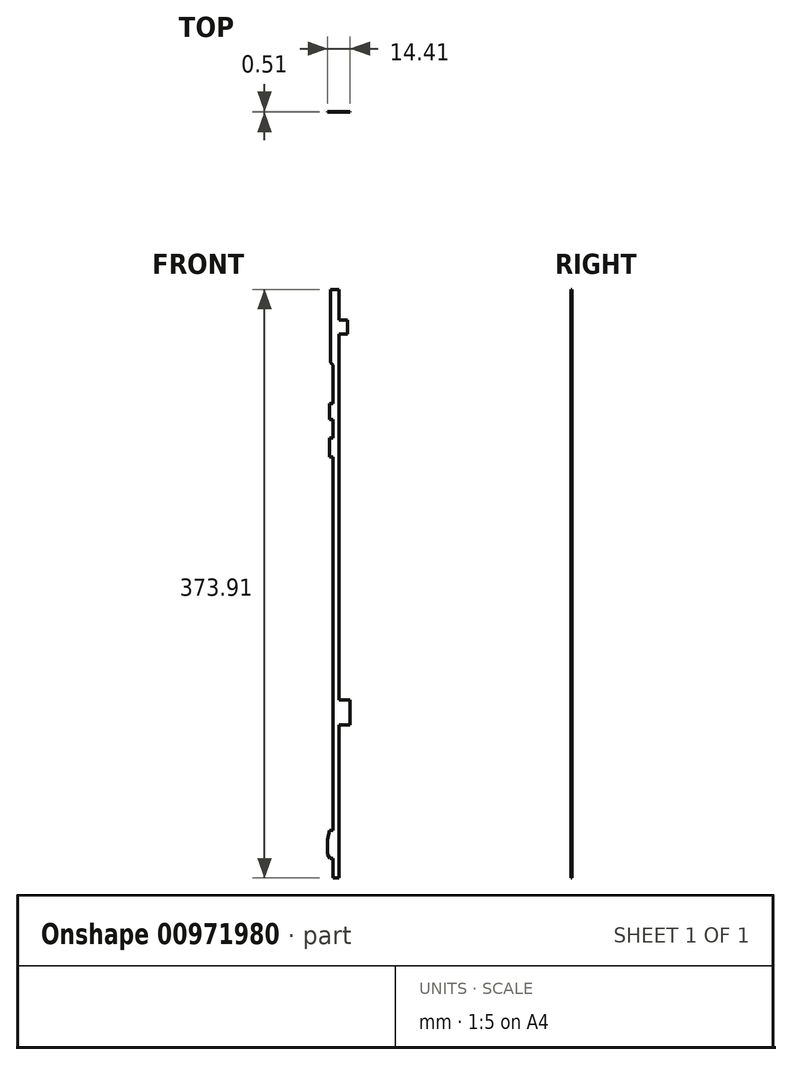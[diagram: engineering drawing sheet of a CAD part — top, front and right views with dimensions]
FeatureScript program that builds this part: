
annotation { "Feature Type Name" : "Feature", "Feature Type Description" : "" }
export const myFeature = defineFeature(function(context is Context, id is Id, definition is map)
    precondition{}
    {
        {
            var Q0;
            Q0=qCreatedBy(makeId("Front.planeOp"),FACE);
            var sketch = newSketch(context, id + "F0", { "sketchPlane" : qUnion([Q0])});
            skLineSegment(sketch, "E0.bottom", {"start": v(2.02, -162.96) * mm, "end": v(-2.02, -162.96) * mm});
            skLineSegment(sketch, "E0.top", {"start": v(2.02, 162.96) * mm, "end": v(-2.02, 162.96) * mm});
            skLineSegment(sketch, "E0.left", {"start": v(2.02, -162.96) * mm, "end": v(2.02, 162.96) * mm});
            skLineSegment(sketch, "E0.right", {"start": v(-2.02, -162.96) * mm, "end": v(-2.02, 162.96) * mm});
            skPoint(sketch, "E0.middle", {"position": v(0, 0) * mm});
            skLineSegment(sketch, "E1", {"start": v(-2.02, 162.96) * mm, "end": v(-3.57, 164.64) * mm});
            skLineSegment(sketch, "E2", {"start": v(-3.57, 164.64) * mm, "end": v(-3.57, 210.95) * mm});
            skLineSegment(sketch, "E3", {"start": v(2.02, 162.96) * mm, "end": v(2.02, 210.95) * mm});
            skLineSegment(sketch, "E4", {"start": v(2.02, 210.95) * mm, "end": v(-3.57, 210.95) * mm});
            skLineSegment(sketch, "E5.bottom", {"start": v(7.35, 191.36) * mm, "end": v(-3.3, 191.36) * mm});
            skLineSegment(sketch, "E5.top", {"start": v(7.35, 182.55) * mm, "end": v(-3.3, 182.55) * mm});
            skLineSegment(sketch, "E5.left", {"start": v(7.35, 191.36) * mm, "end": v(7.35, 182.55) * mm});
            skLineSegment(sketch, "E5.right", {"start": v(-3.3, 191.36) * mm, "end": v(-3.3, 182.55) * mm});
            skPoint(sketch, "E5.middle", {"position": v(2.02, 186.95) * mm});
            skLineSegment(sketch, "E6", {"start": v(-3.57, 138.46) * mm, "end": v(-2.02, 138.46) * mm});
            skLineSegment(sketch, "E7.bottom", {"start": v(-2.02, 138.46) * mm, "end": v(-4.03, 138.46) * mm});
            skLineSegment(sketch, "E7.top", {"start": v(-2.02, 128.28) * mm, "end": v(-4.03, 128.28) * mm});
            skLineSegment(sketch, "E7.left", {"start": v(-2.02, 138.46) * mm, "end": v(-2.02, 128.28) * mm});
            skLineSegment(sketch, "E7.right", {"start": v(-4.03, 138.46) * mm, "end": v(-4.03, 128.28) * mm});
            skLineSegment(sketch, "E8", {"start": v(-2.02, 128.28) * mm, "end": v(-2.02, 116.47) * mm});
            skLineSegment(sketch, "E9.bottom", {"start": v(-2.02, 116.47) * mm, "end": v(-4.03, 116.47) * mm});
            skLineSegment(sketch, "E9.top", {"start": v(-2.02, 104.66) * mm, "end": v(-4.03, 104.66) * mm});
            skLineSegment(sketch, "E9.left", {"start": v(-2.02, 116.47) * mm, "end": v(-2.02, 104.66) * mm});
            skLineSegment(sketch, "E9.right", {"start": v(-4.03, 116.47) * mm, "end": v(-4.03, 104.66) * mm});
            skLineSegment(sketch, "E10.bottom", {"start": v(2.02, -49.96) * mm, "end": v(9.03, -49.96) * mm});
            skLineSegment(sketch, "E10.top", {"start": v(2.02, -65.65) * mm, "end": v(9.03, -65.65) * mm});
            skLineSegment(sketch, "E10.left", {"start": v(2.02, -49.96) * mm, "end": v(2.02, -65.65) * mm});
            skLineSegment(sketch, "E10.right", {"start": v(9.03, -49.96) * mm, "end": v(9.03, -65.65) * mm});
            skLineSegment(sketch, "E11", {"start": v(2.02, -65.65) * mm, "end": v(-2.02, -65.65) * mm});
            skLineSegment(sketch, "E12", {"start": v(-2.02, -65.65) * mm, "end": v(-2.02, -132.81) * mm});
            skLineSegment(sketch, "E13", {"start": v(-2.02, -132.81) * mm, "end": v(-4.03, -132.81) * mm});
            skLineSegment(sketch, "E14", {"start": v(-4.03, -132.81) * mm, "end": v(-5.38, -138.76) * mm});
            skLineSegment(sketch, "E15", {"start": v(-5.38, -138.76) * mm, "end": v(-5.38, -147.79) * mm});
            skLineSegment(sketch, "E16", {"start": v(-5.38, -147.79) * mm, "end": v(-3.72, -150.6) * mm});
            skLineSegment(sketch, "E17", {"start": v(-3.72, -150.6) * mm, "end": v(-2.02, -150.6) * mm});
            skSolve(sketch);
        }
        {
            var Q0;
            Q0=makeQuery(id+"F0.imprint","IMPRINT",FACE,{"disambiguationData":[TD([[makeQuery(id+"F0.imprint","IMPRINT",EDGE,{"derivedFrom":sQuery(id+"F0.wireOp",EDGE,"E10.bottom")}),-1.0]])]});
            var Q1;
            {var subQ0=sQuery(id+"F0.wireOp",EDGE,"E13");Q1=makeQuery(id+"F0.imprint","IMPRINT",FACE,{"disambiguationData":[TD([[makeQuery(id+"F0.imprint","IMPRINT",EDGE,{"derivedFrom":subQ0}),1.0]])]});}
            var Q2;
            {var subQ5=sQuery(id+"F0.wireOp",EDGE,"E5.left");Q2=makeQuery(id+"F0.imprint","IMPRINT",FACE,{"disambiguationData":[TD([[makeQuery(id+"F0.imprint","IMPRINT",EDGE,{"derivedFrom":subQ5}),-1.0]])]});}
            var Q3;
            {var subQ5=sQuery(id+"F0.wireOp",EDGE,"E5.right");Q3=makeQuery(id+"F0.imprint","IMPRINT",FACE,{"disambiguationData":[TD([[makeQuery(id+"F0.imprint","IMPRINT",EDGE,{"derivedFrom":subQ5}),1.0]])]});}
            var Q4;
            {var subQ1=sQuery(id+"F0.wireOp",EDGE,"E0.top");Q4=makeQuery(id+"F0.imprint","IMPRINT",FACE,{"disambiguationData":[TD([[makeQuery(id+"F0.imprint","IMPRINT",EDGE,{"derivedFrom":subQ1}),-1.0]])]});}
            var Q5;
            {var subQ1=sQuery(id+"F0.wireOp",EDGE,"E0.top");Q5=makeQuery(id+"F0.imprint","IMPRINT",FACE,{"disambiguationData":[TD([[makeQuery(id+"F0.imprint","IMPRINT",EDGE,{"derivedFrom":subQ1}),1.0]])]});}
            var Q6;
            Q6=makeQuery(id+"F0.imprint","IMPRINT",FACE,{"disambiguationData":[TD([[makeQuery(id+"F0.imprint","IMPRINT",EDGE,{"derivedFrom":sQuery(id+"F0.wireOp",EDGE,"E9.bottom")}),1.0]])]});
            var Q7;
            {var subQ1=sQuery(id+"F0.wireOp",EDGE,"E0.bottom");Q7=makeQuery(id+"F0.imprint","IMPRINT",FACE,{"disambiguationData":[TD([[makeQuery(id+"F0.imprint","IMPRINT",EDGE,{"derivedFrom":subQ1}),-1.0]])]});}
            var Q8;
            Q8=makeQuery(id+"F0.imprint","IMPRINT",FACE,{"disambiguationData":[TD([[makeQuery(id+"F0.imprint","IMPRINT",EDGE,{"derivedFrom":sQuery(id+"F0.wireOp",EDGE,"E7.top")}),-1.0]])]});
            extrude(context, id + "F1", {"entities" : qUnion([Q0, Q1, Q2, Q3, Q4, Q5, Q6, Q7, Q8]), "depth" : 0.5 * mm, "offsetDistance" : 25.4 * mm});
        }
    });
